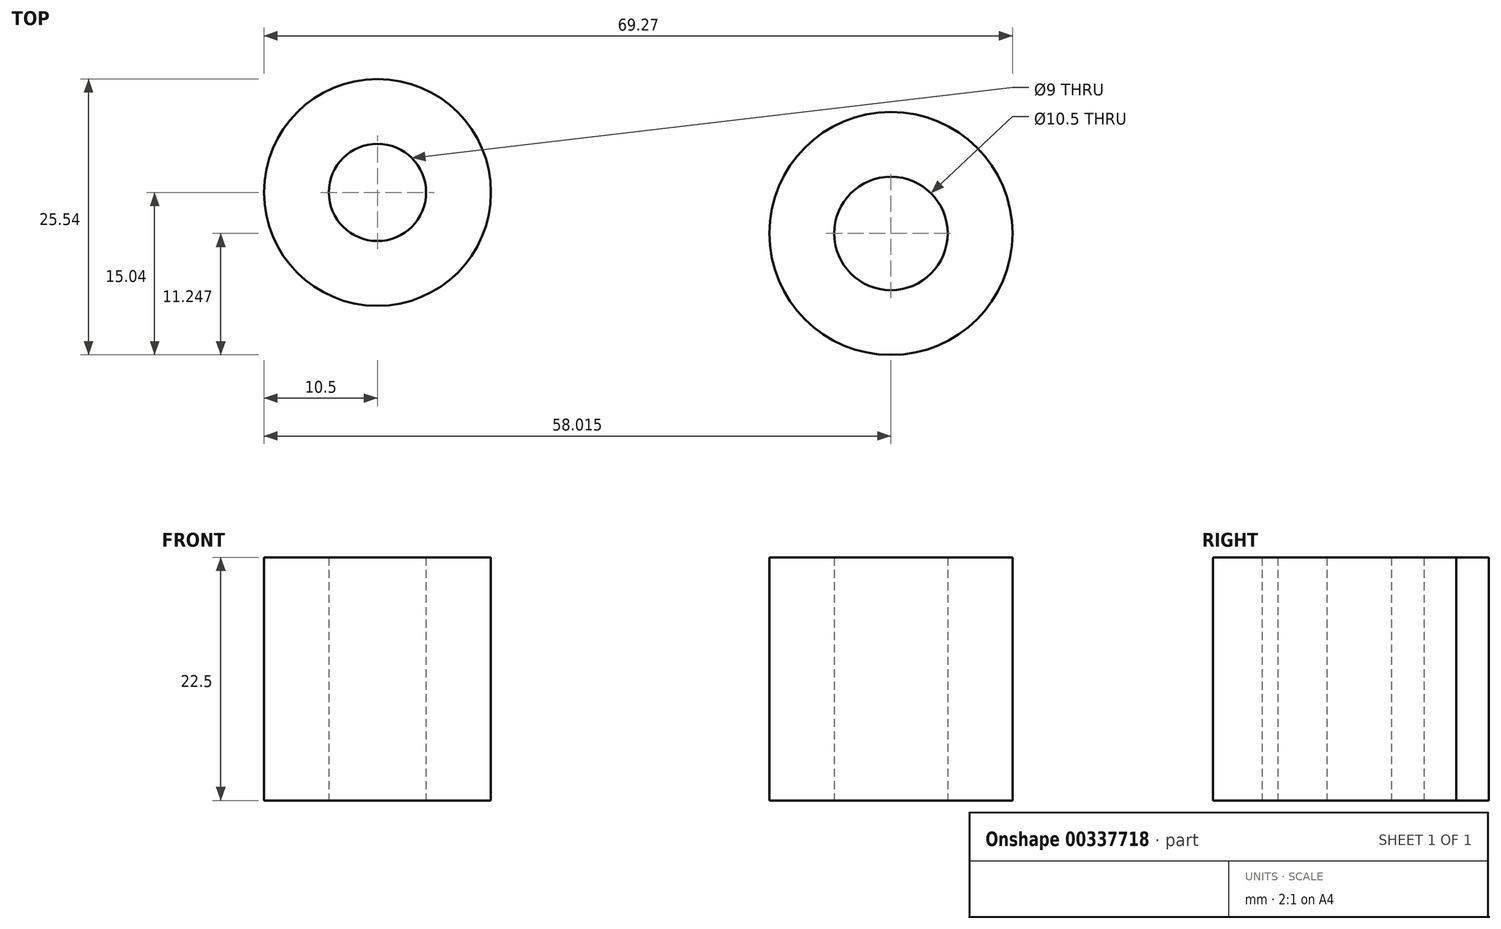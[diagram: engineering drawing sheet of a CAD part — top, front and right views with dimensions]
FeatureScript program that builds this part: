
annotation { "Feature Type Name" : "Feature", "Feature Type Description" : "" }
export const myFeature = defineFeature(function(context is Context, id is Id, definition is map)
    precondition{}
    {
        {
            var Q0;
            Q0=qCreatedBy(makeId("Top.planeOp"),FACE);
            var sketch = newSketch(context, id + "F0", { "sketchPlane" : qUnion([Q0])});
            skCircle(sketch, "E0", {"center": v(0, 0) * mm, "radius": 10.5 * mm});
            skCircle(sketch, "E1", {"center": v(0, 0) * mm, "radius": 4.5 * mm});
            skCircle(sketch, "E2", {"center": v(47.52, -3.8) * mm, "radius": 11.25 * mm});
            skCircle(sketch, "E3", {"center": v(47.52, -3.8) * mm, "radius": 5.25 * mm});
            skSolve(sketch);
        }
        {
            var Q0;
            Q0=makeQuery(id+"F0.imprint","IMPRINT",FACE,{"disambiguationData":[TD([[makeQuery(id+"F0.imprint","IMPRINT",EDGE,{"derivedFrom":sQuery(id+"F0.wireOp",EDGE,"E0")}),1.0]])]});
            var Q1;
            Q1=makeQuery(id+"F0.imprint","IMPRINT",FACE,{"disambiguationData":[TD([[makeQuery(id+"F0.imprint","IMPRINT",EDGE,{"derivedFrom":sQuery(id+"F0.wireOp",EDGE,"E2")}),1.0]])]});
            extrude(context, id + "F1", {"entities" : qUnion([Q0, Q1]), "depth" : 22.5 * mm});
        }
    });
